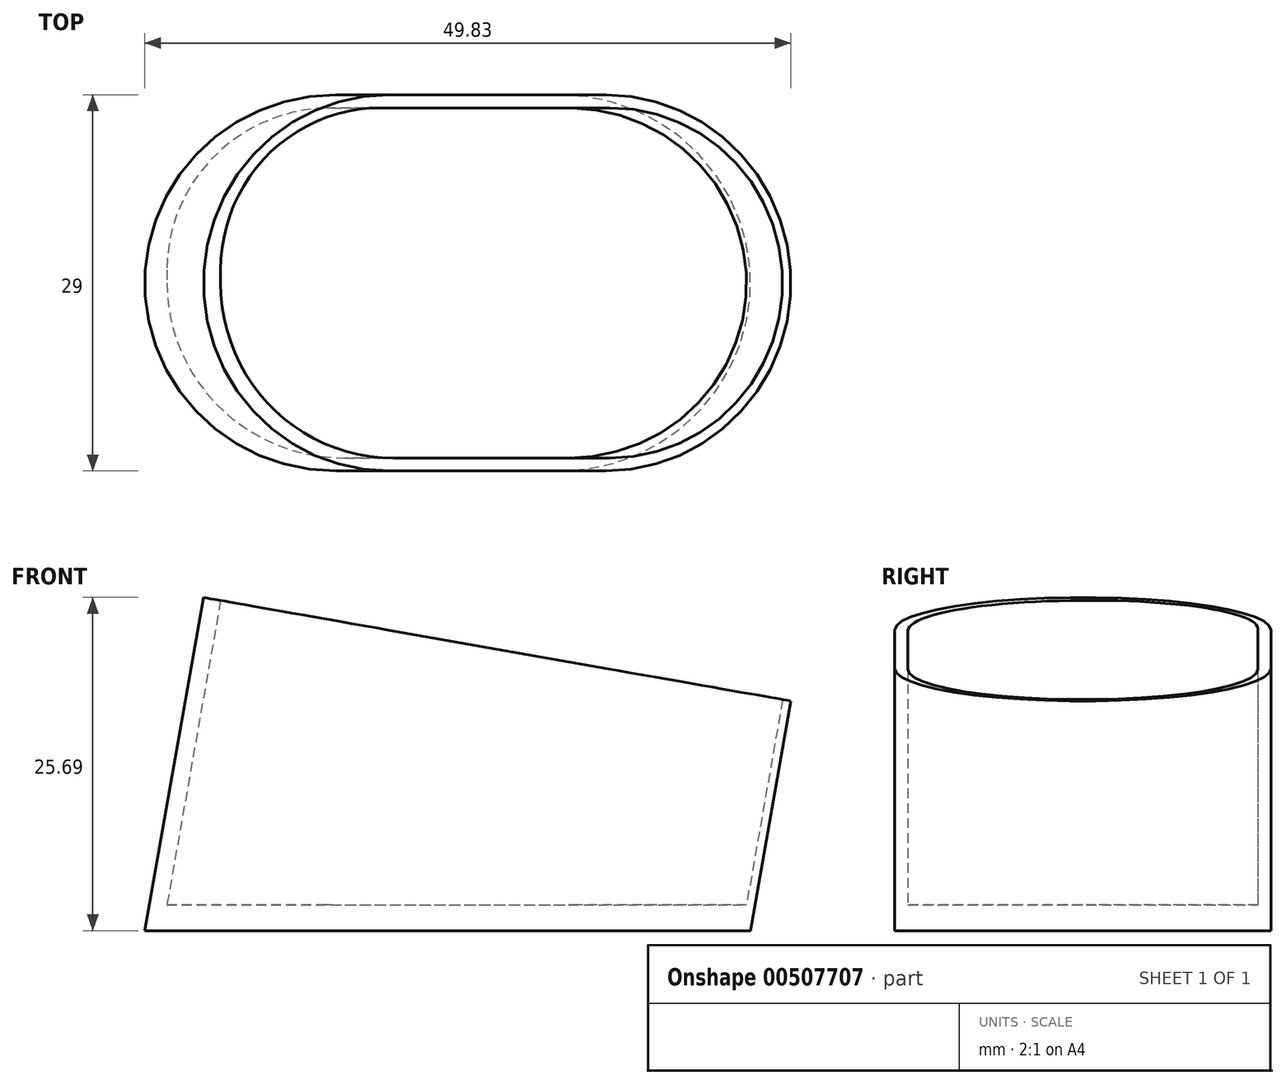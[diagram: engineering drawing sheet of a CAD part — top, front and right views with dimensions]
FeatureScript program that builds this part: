
annotation { "Feature Type Name" : "Feature", "Feature Type Description" : "" }
export const myFeature = defineFeature(function(context is Context, id is Id, definition is map)
    precondition{}
    {
        {
            var Q0;
            Q0=qCreatedBy(makeId("Right.planeOp"),FACE);
            var sketch = newSketch(context, id + "F0", { "sketchPlane" : qUnion([Q0])});
            skLineSegment(sketch, "E0", {"start": v(-17.57, 2) * mm, "end": v(24.1, 2) * mm});
            skSolve(sketch);
        }
        {
            var Q0;
            Q0 = qBodyType(qCreatedBy(id + "F0" ,EDGE), BodyType.WIRE);
            cPlane(context, id + "F1", {"entities" : qUnion([Q0]), "cplaneType" : CPlaneType.LINE_ANGLE, "offset" : 25 * mm, "angle" : 10 * degree, "width" : 150 * mm, "height" : 150 * mm});
        }
        {
            var Q0;
            Q0=qCreatedBy(id+"F1.planeOp",FACE);
            var sketch = newSketch(context, id + "F2", { "sketchPlane" : qUnion([Q0])});
            skLineSegment(sketch, "E1.bottom", {"start": v(-9.5, 13.5) * mm, "end": v(8.5, 13.5) * mm});
            skLineSegment(sketch, "E1.top", {"start": v(-8.5, -13.5) * mm, "end": v(8.5, -13.5) * mm});
            skLineSegment(sketch, "E1.left", {"start": v(-22, 1) * mm, "end": v(-22, 0) * mm});
            skLineSegment(sketch, "E1.right", {"start": v(22, 0) * mm, "end": v(22, 0) * mm});
            skPoint(sketch, "E1.middle", {"position": v(0, 0) * mm});
            skPoint(sketch, "E2.visualSharp", {"position": v(-22, 13.5) * mm});
            skArc(sketch, "E2.filletArc", {"start": v(-9.5, 13.5) * mm, "mid": v(-18.34, 9.84) * mm, "end": v(-22, 1) * mm});
            skPoint(sketch, "E3.visualSharp", {"position": v(22, 13.5) * mm});
            skArc(sketch, "E3.filletArc", {"start": v(22, 0) * mm, "mid": v(18.05, 9.55) * mm, "end": v(8.5, 13.5) * mm});
            skPoint(sketch, "E4.visualSharp", {"position": v(22, -13.5) * mm});
            skArc(sketch, "E4.filletArc", {"start": v(8.5, -13.5) * mm, "mid": v(18.05, -9.55) * mm, "end": v(22, 0) * mm});
            skPoint(sketch, "E5.visualSharp", {"position": v(-22, -13.5) * mm});
            skArc(sketch, "E5.filletArc", {"start": v(-22, 0) * mm, "mid": v(-18.05, -9.55) * mm, "end": v(-8.5, -13.5) * mm});
            skSolve(sketch);
        }
        {
            var Q0;
            Q0=qCreatedBy(id+"F1.planeOp",FACE);
            var sketch = newSketch(context, id + "F3", { "sketchPlane" : qUnion([Q0])});
            skLineSegment(sketch, "E6.bottom", {"start": v(-8.85, 14.5) * mm, "end": v(8.15, 14.5) * mm});
            skLineSegment(sketch, "E6.top", {"start": v(-8.85, -14.5) * mm, "end": v(8.15, -14.5) * mm});
            skLineSegment(sketch, "E6.left", {"start": v(-23.35, 0) * mm, "end": v(-23.35, 0) * mm});
            skLineSegment(sketch, "E6.right", {"start": v(22.65, 0) * mm, "end": v(22.65, 0) * mm});
            skPoint(sketch, "E6.middle", {"position": v(-0.35, 0) * mm});
            skPoint(sketch, "E7.visualSharp", {"position": v(-23.35, 14.5) * mm});
            skArc(sketch, "E7.filletArc", {"start": v(-8.85, 14.5) * mm, "mid": v(-19.1, 10.25) * mm, "end": v(-23.35, 0) * mm});
            skPoint(sketch, "E8.visualSharp", {"position": v(22.65, 14.5) * mm});
            skArc(sketch, "E8.filletArc", {"start": v(22.65, 0) * mm, "mid": v(18.4, 10.25) * mm, "end": v(8.15, 14.5) * mm});
            skPoint(sketch, "E9.visualSharp", {"position": v(22.65, -14.5) * mm});
            skArc(sketch, "E9.filletArc", {"start": v(8.15, -14.5) * mm, "mid": v(18.4, -10.25) * mm, "end": v(22.65, 0) * mm});
            skPoint(sketch, "E10.visualSharp", {"position": v(-23.35, -14.5) * mm});
            skArc(sketch, "E10.filletArc", {"start": v(-23.35, 0) * mm, "mid": v(-19.1, -10.25) * mm, "end": v(-8.85, -14.5) * mm});
            skSolve(sketch);
        }
        {
            var Q0;
            Q0 = qSketchRegion(id + "F3", true);
            extrude(context, id + "F4", {"entities" : qUnion([Q0]), "endBound" : BoundingType.SYMMETRIC, "depth" : 40 * mm});
        }
        {
            var Q0;
            Q0 = qSketchRegion(id + "F2", true);
            extrude(context, id + "F5", {"entities" : qUnion([Q0]), "operationType" : NewBodyOperationType.REMOVE, "endBound" : BoundingType.SYMMETRIC, "depth" : 40 * mm});
        }
        {
            var Q0;
            Q0=qCreatedBy(makeId("Top.planeOp"),FACE);
            var sketch = newSketch(context, id + "F6", { "sketchPlane" : qUnion([Q0])});
            skLineSegment(sketch, "E11.bottom", {"start": v(-9.75, 13.5) * mm, "end": v(9.25, 13.5) * mm});
            skLineSegment(sketch, "E11.top", {"start": v(-9.75, -13.5) * mm, "end": v(9.25, -13.5) * mm});
            skLineSegment(sketch, "E11.left", {"start": v(-22.75, 0.5) * mm, "end": v(-22.75, -0.5) * mm});
            skLineSegment(sketch, "E11.right", {"start": v(22.75, 0) * mm, "end": v(22.75, 0) * mm});
            skPoint(sketch, "E11.middle", {"position": v(0, 0) * mm});
            skPoint(sketch, "E12.visualSharp", {"position": v(-22.75, 13.5) * mm});
            skArc(sketch, "E12.filletArc", {"start": v(-9.75, 13.5) * mm, "mid": v(-18.94, 9.7) * mm, "end": v(-22.75, 0.5) * mm});
            skPoint(sketch, "E13.visualSharp", {"position": v(22.75, 13.5) * mm});
            skArc(sketch, "E13.filletArc", {"start": v(22.75, 0) * mm, "mid": v(18.8, 9.55) * mm, "end": v(9.25, 13.5) * mm});
            skPoint(sketch, "E14.visualSharp", {"position": v(22.75, -13.5) * mm});
            skArc(sketch, "E14.filletArc", {"start": v(9.25, -13.5) * mm, "mid": v(18.8, -9.55) * mm, "end": v(22.75, 0) * mm});
            skPoint(sketch, "E15.visualSharp", {"position": v(-22.75, -13.5) * mm});
            skArc(sketch, "E15.filletArc", {"start": v(-22.75, -0.5) * mm, "mid": v(-18.94, -9.7) * mm, "end": v(-9.75, -13.5) * mm});
            skSolve(sketch);
        }
        {
            var Q0;
            Q0=qCreatedBy(makeId("Top.planeOp"),FACE);
            var sketch = newSketch(context, id + "F7", { "sketchPlane" : qUnion([Q0])});
            skLineSegment(sketch, "E16.bottom", {"start": v(-28.36, 18.97) * mm, "end": v(28.36, 18.97) * mm});
            skLineSegment(sketch, "E16.top", {"start": v(-28.36, -18.97) * mm, "end": v(28.36, -18.97) * mm});
            skLineSegment(sketch, "E16.left", {"start": v(-28.36, 18.97) * mm, "end": v(-28.36, -18.97) * mm});
            skLineSegment(sketch, "E16.right", {"start": v(28.36, 18.97) * mm, "end": v(28.36, -18.97) * mm});
            skPoint(sketch, "E16.middle", {"position": v(0, 0) * mm});
            skSolve(sketch);
        }
        {
            var Q0;
            Q0 = qSketchRegion(id + "F7", true);
            extrude(context, id + "F8", {"entities" : qUnion([Q0]), "operationType" : NewBodyOperationType.REMOVE, "oppositeDirection" : true, "depth" : 25 * mm});
        }
        {
            var Q0;
            Q0 = qSketchRegion(id + "F6", true);
            extrude(context, id + "F9", {"entities" : qUnion([Q0]), "operationType" : NewBodyOperationType.ADD, "depth" : 2 * mm});
        }
    });
